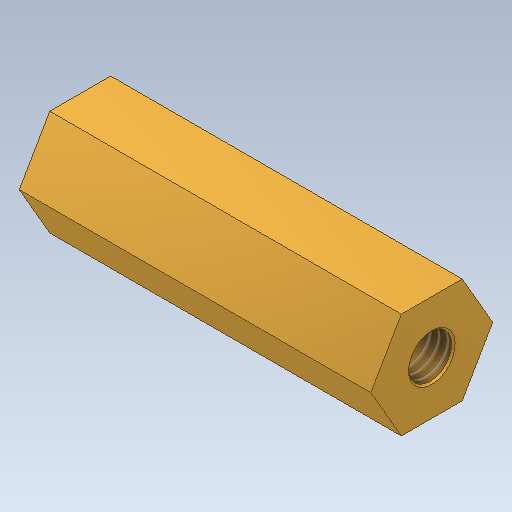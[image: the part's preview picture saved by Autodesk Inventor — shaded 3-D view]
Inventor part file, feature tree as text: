
AUTODESK INVENTOR PART (.ipt)
format: ipt  version: 2021 (Build 250183000, 183)  size: 135,680 bytes
history: native  units: mm
features: thread x6, other x5, chamfer x3, revolve x1
ambient origin geometry x6: Origin, XZ Plane, XY Plane, X Axis, Y Axis, Z Axis
bodies: Solid1 (feature_tree)
feature tree (15):
  revolve  "Revolution1"  [1 undecoded]
  other  "N-Side1"
  thread  "Thread2"  [1 undecoded]
  thread  "Thread6"  [1 undecoded]
  thread  "Thread4"  [1 undecoded]
  other  "Start Plane"
  other  "Origin point"
  other  "Main Sketch"
  other  "iFeature1:1"
  thread  "Thread1"  [1 undecoded]
  chamfer  "Chamfer1"  Distance=6.0mm
  thread  "Thread3"  [1 undecoded]
  chamfer  "Chamfer2"  Distance=6.0mm
  thread  "Thread5"  [1 undecoded]
  chamfer  "Chamfer3"  Distance=2.459mm
note: 7 required parameter values undecoded (feature->parameter linkage not recoverable at this tier; creation-order binding heuristic only, values carry confidence <= 0.55)